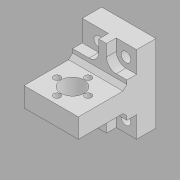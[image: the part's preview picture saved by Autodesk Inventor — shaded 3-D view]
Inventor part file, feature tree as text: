
AUTODESK INVENTOR PART (.ipt)
format: ipt  version: 2020.2 (Build 242310000, 310)  size: 193,024 bytes
history: native  units: mm
features: extrude x4, sketch x3, mirror x2, hole x1, direct_edit x1, chamfer x1, move_body x1
ambient origin geometry x8: Origin, YZ Plane, XZ Plane, XY Plane, X Axis, Y Axis, Z Axis, Center Point
bodies: Solid1 (feature_tree)
feature tree (13):
  extrude  "Extrusion1"  Depth=25.0mm
  hole  "Hole1"  [1 undecoded]
  extrude  "Extrusion3"  Depth=6.0mm
  extrude  "Extrusion4"  Depth=6.0mm
  extrude  "Extrusion5"  Depth=25.0mm
  mirror  "Mirror1"
  mirror  "Mirror2"
  direct_edit  "Direct Edit1"
  chamfer  "Chamfer2"  Distance=25.0mm
  sketch  "Sketch1"  dims[d0=40.0mm d1=25.0mm]
  sketch  "Sketch4"  dims[d2=15.0mm d3=0.0mm]
  sketch  "Sketch5"  dims[d9=5.0mm d10=6.0mm d11=10.0mm d12=5.0mm d13=90.0deg d14=8.0mm d15=20.594885mm d20=10.0mm d21=6.0mm d22=6.0mm d24=5.5mm d25=25.0mm d26=0.0mm d27=12.0mm d28=12.0mm d29=15.0mm d30=3.5mm d31=8.0mm d32=40.0mm d34=360.0deg d36=0.0mm d37=0.0mm d39=25.0mm d40=0.0mm d41=0.0mm d42=0.0mm d43=3.0mm d44=2.0mm d45=2.0mm d46=45.0deg]
  move_body  "Move1"
note: 1 required parameter value undecoded (feature->parameter linkage not recoverable at this tier; creation-order binding heuristic only, values carry confidence <= 0.55)
